# Revit family: TY4234
name_source: partatom
category: Sprinklers
revit_build: Autodesk Revit 2016 (Build: 20150220_1215(x64)
units: mm (PartAtom-declared; Revit-internal decimal feet)

## family parameters
Always vertical = Yes
Cut with Voids When Loaded = No
Maintain Annotation Orientation = No
OmniClass Number = 23.65.70.17.11.24
OmniClass Title = Fire Fighting Sprinkler Heads
Part Type = Normal
Room Calculation Point = No
Round Connector Dimension = Use Diameter
Shared = No
Work Plane-Based = No

## types (6) — shared parameters
COBie = Yes
COBie.Component.Name = Sprinklers:Pendent_SIN
COBie.Type = Yes
COBie.Type.AssetType = Fixed
COBie.Type.Category = Pr_70_55_97_84:Sprinklers
COBie.Type.DurationUnit = year
COBie.Type.Manufacturer = Tyco Fire Protection Products
COBie.Type.Material = Brass
COBie.Type.NominalHeight = 0' - 0"
COBie.Type.NominalLength = 0' - 0"
COBie.Type.NominalWidth = 0' - 0"
COBie.Type.Shape = Cylinder
COBie.Type.Size = 3/4"(DN20)
Coverage = Standard
K-Factor = 6.9019
Manufacturer = Tyco Fire Protection Products
Manufacturer URL = www.tyco-fire.com
Model = LFII
Nominal Diameter 1 = 1"
Orifice = Extra Large
Orifice Size = 1"
Outside Diameter 1 = 1"
Response = Quick
SIN No = TY4234
Takeout 1 = 2"
Technical Data Sheet No = TFP408
zero-valued in all types: COBie.Type.ReplacementCost, Style Id

## per-type parameters (varying)
| type | COBie.Component.Description | COBie.Type.Colour | COBie.Type.Finish | COBie.Type.ModelNumber | COBie.Type.ModelReference | COBie.Type.WarrantyGuarantorParts | Part No | Temperature Rating |
| LFII - Resid. NFPA 13 Opt. Pendent, Rec. Sprinkler 3/4" NPT K=6.9 155°F/68°C Brass TY4234 TFP408_51-069-1-155 | LFII Wet Pendent  68.3°C K99.5 DN20 NPT Br | Yellow | Natural Brass | 51-069-1-155 | LFII Wet Pendent  68.3°C K99.5 DN20 NPT Br | http://tycofsbp.com | 51-069-1-155 | 155 °F |
| LFII - Resid. NFPA 13 Opt. Pendent, Rec. Sprinkler 3/4" NPT K=6.9 175°F/79°C Brass TY4234 TFP408_51-069-1-175 | LFII Wet Pendent  79.4°C K99.5 DN20 NPT Br | Yellow | Natural Brass | 51-069-1-175 | LFII Wet Pendent  79.4°C K99.5 DN20 NPT Br | http://tycofsbp.com
TFPPTerms_of_Sale.pdf | 51-069-1-175 | 175 °F |
| LFII - Resid. NFPA 13 Opt. Pendent, Rec. Sprinkler 3/4" NPT K=6.9 155°F/68°C White TY4234 TFP408_51-069-4-155 | LFII Wet Pendent  68.3°C K99.5 DN20 NPT Wh | White | Signal White | 51-069-4-155 | LFII Wet Pendent  68.3°C K99.5 DN20 NPT Wh | http://tycofsbp.com
TFPPTerms_of_Sale.pdf | 51-069-4-155 | 155 °F |
| LFII - Resid. NFPA 13 Opt. Pendent, Rec. Sprinkler 3/4" NPT K=6.9 175°F/79°C White TY4234 TFP408_51-069-4-175 | LFII Wet Pendent  79.4°C K99.5 DN20 NPT Wh | White | Signal White | 51-069-4-175 | LFII Wet Pendent  79.4°C K99.5 DN20 NPT Wh | http://tycofsbp.com
TFPPTerms_of_Sale.pdf | 51-069-4-175 | 175 °F |
| LFII - Resid. NFPA 13 Opt. Pendent, Rec. Sprinkler 3/4" NPT K=6.9 155°F/68°C Chrome TY4234 TFP408_51-069-9-155 | LFII Wet Pendent  68.3°C K99.5 DN20 NPT Chr | Silver | Chrome Plated | 51-069-9-155 | LFII Wet Pendent  68.3°C K99.5 DN20 NPT Chr | http://tycofsbp.com
TFPPTerms_of_Sale.pdf | 51-069-9-155 | 155 °F |
| LFII - Resid. NFPA 13 Opt. Pendent, Rec. Sprinkler 3/4" NPT K=6.9 175°F/79°C Chrome TY4234 TFP408_51-069-9-175 | LFII Wet Pendent  79.4°C K99.5 DN20 NPT Chr | Silver | Chrome Plated | 51-069-9-175 | LFII Wet Pendent  79.4°C K99.5 DN20 NPT Chr | http://tycofsbp.com
TFPPTerms_of_Sale.pdf | 51-069-9-175 | 175 °F |

note: column(s) folded — value = type name in every type: Description

## geometry (parser evidence)
native form markers: Blend x4, Sweep x45
no freeform markers — native parametric forms only
